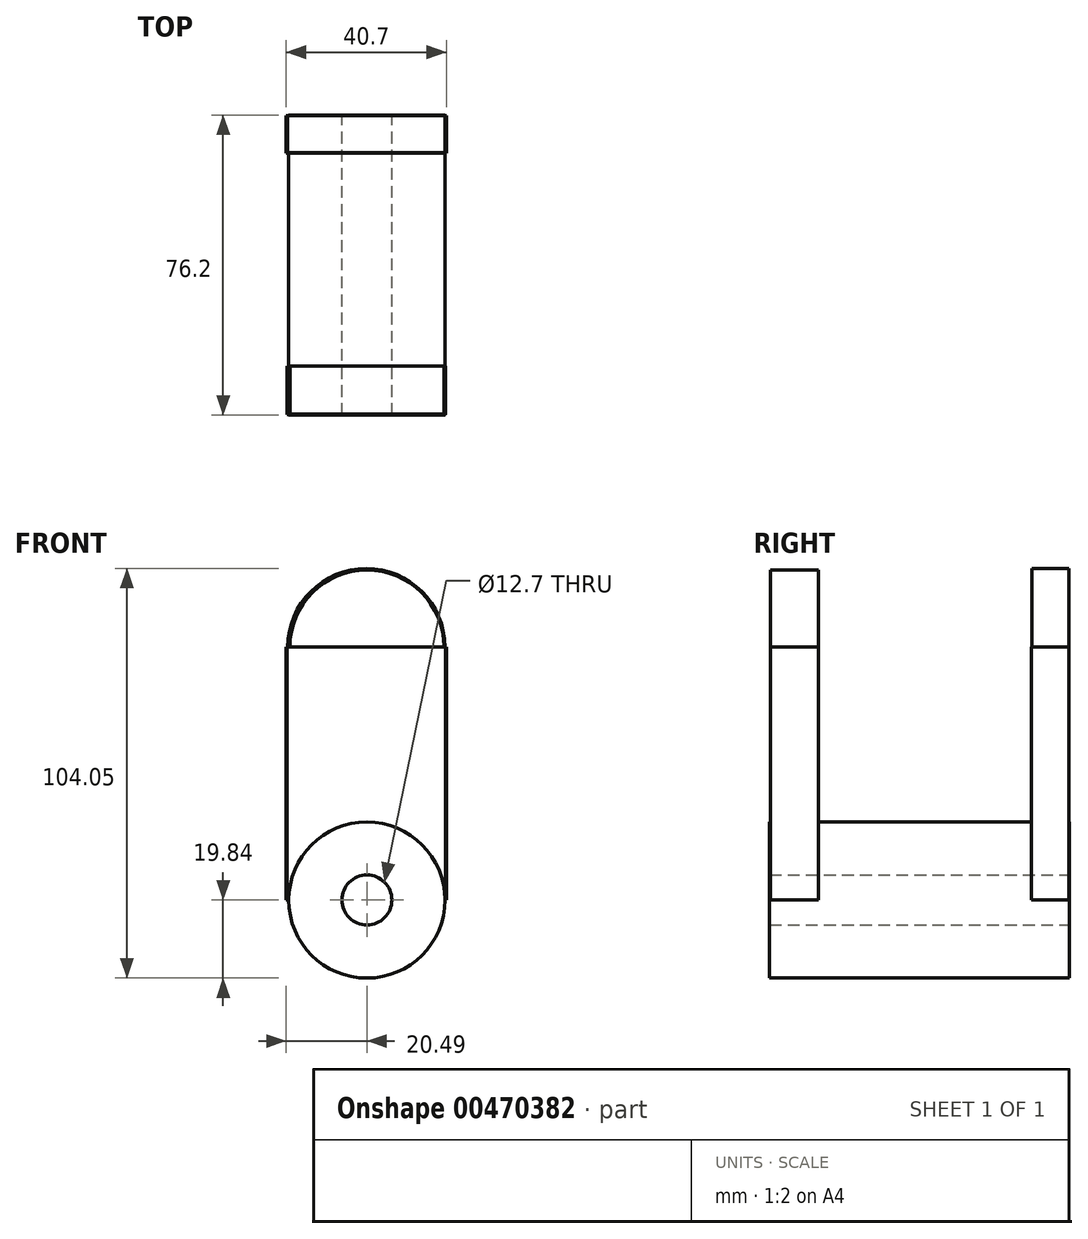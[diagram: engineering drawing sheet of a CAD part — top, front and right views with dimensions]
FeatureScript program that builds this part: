
annotation { "Feature Type Name" : "Feature", "Feature Type Description" : "" }
export const myFeature = defineFeature(function(context is Context, id is Id, definition is map)
    precondition{}
    {
        {
            var Q0;
            Q0=qCreatedBy(makeId("Front.planeOp"),FACE);
            var sketch = newSketch(context, id + "F0", { "sketchPlane" : qUnion([Q0])});
            skCircle(sketch, "E0", {"center": v(0, 0) * mm, "radius": 19.84 * mm});
            skSolve(sketch);
        }
        {
            var Q0;
            Q0 = qSketchRegion(id + "F0", true);
            extrude(context, id + "F1", {"entities" : qUnion([Q0]), "depth" : 76.2 * mm, "symmetric" : true});
        }
        {
            var Q0;
            Q0=makeQuery(id+"F1.opExtrude","CAP_FACE",FACE,{"disambiguationData":[OSD([sQuery(id+"F0.wireOp",EDGE,"E0")])],"isStart":true});
            var sketch = newSketch(context, id + "F2", { "sketchPlane" : qUnion([Q0])});
            skPoint(sketch, "E1", {"position": v(0, 0) * mm});
            skSolve(sketch);
        }
        {
            var Q0;
            Q0=qCreatedBy(makeId("Top.planeOp"),FACE);
            var sketch = newSketch(context, id + "F3", { "sketchPlane" : qUnion([Q0])});
            skLineSegment(sketch, "E2.bottom", {"start": v(-20.21, -37.91) * mm, "end": v(19.93, -37.91) * mm});
            skLineSegment(sketch, "E2.top", {"start": v(-20.21, -25.65) * mm, "end": v(19.93, -25.65) * mm});
            skLineSegment(sketch, "E2.left", {"start": v(-20.21, -37.91) * mm, "end": v(-20.21, -25.65) * mm});
            skLineSegment(sketch, "E2.right", {"start": v(19.93, -37.91) * mm, "end": v(19.93, -25.65) * mm});
            skSolve(sketch);
        }
        {
            var Q0;
            Q0=makeQuery(id+"F3.imprint","IMPRINT",FACE,{"disambiguationData":[TD([[makeQuery(id+"F3.imprint","IMPRINT",EDGE,{"derivedFrom":sQuery(id+"F3.wireOp",EDGE,"E2.bottom")}),1.0]])]});
            extrude(context, id + "F4", {"entities" : qUnion([Q0]), "operationType" : NewBodyOperationType.ADD, "depth" : 64.26 * mm});
        }
        {
            var Q0;
            Q0=qCreatedBy(makeId("Top.planeOp"),FACE);
            var sketch = newSketch(context, id + "F5", { "sketchPlane" : qUnion([Q0])});
            skLineSegment(sketch, "E3.bottom", {"start": v(-20.5, 28.44) * mm, "end": v(20.21, 28.44) * mm});
            skLineSegment(sketch, "E3.top", {"start": v(-20.5, 37.91) * mm, "end": v(20.21, 37.91) * mm});
            skLineSegment(sketch, "E3.left", {"start": v(-20.5, 28.44) * mm, "end": v(-20.5, 37.91) * mm});
            skLineSegment(sketch, "E3.right", {"start": v(20.21, 28.44) * mm, "end": v(20.21, 37.91) * mm});
            skSolve(sketch);
        }
        {
            var Q0;
            Q0 = qSketchRegion(id + "F5", true);
            extrude(context, id + "F6", {"entities" : qUnion([Q0]), "operationType" : NewBodyOperationType.ADD, "depth" : 64.26 * mm});
        }
        {
            var Q0;
            Q0=sQuery(id+"F2.wireOp",VERTEX,"E1");
            var Q1;
            Q1=makeQuery(id+"F1.opExtrude","SWEPT_BODY",BODY,{"disambiguationData":[OSD([sQuery(id+"F0.wireOp",EDGE,"E0")])]});
            hole(context, id + "F7", {"style" : HoleStyle.SIMPLE, "endStyle" : HoleEndStyle.THROUGH, "holeDiameter" : 12.7 * mm, "isTappedThrough" : true, "tappedDepth" : 12.7 * mm, "tapClearance" : 3, "locations" : qUnion([Q0]), "scope" : qUnion([Q1])});
        }
        {
            var Q0;
            Q0=makeQuery(id+"F4.opExtrude","SWEPT_FACE",FACE,{"disambiguationData":[OSD([sQuery(id+"F3.wireOp",EDGE,"E2.top")])]});
            var sketch = newSketch(context, id + "F8", { "sketchPlane" : qUnion([Q0])});
            skCircle(sketch, "E4", {"center": v(0, 64.26) * mm, "radius": 19.57 * mm});
            skLineSegment(sketch, "E5", {"start": v(-19.93, 64.26) * mm, "end": v(20.21, 64.26) * mm});
            skSolve(sketch);
        }
        {
            var Q0;
            {var subQ0=sQuery(id+"F8.wireOp",EDGE,"E5");var subQ1=sQuery(id+"F8.wireOp",EDGE,"E4");var subQ2=makeQuery(id+"F8.imprint","INTERSECT",VERTEX,{"disambiguationData":[OD(0.0)],"derivedFrom":[subQ1,subQ0]});Q0=makeQuery(id+"F8.imprint","IMPRINT",FACE,{"disambiguationData":[TD([[makeQuery(id+"F8.imprint","IMPRINT",EDGE,{"disambiguationData":[TD([[subQ2,-1.0]])],"derivedFrom":subQ1}),1.0]])]});}
            extrude(context, id + "F9", {"entities" : qUnion([Q0]), "operationType" : NewBodyOperationType.ADD, "oppositeDirection" : true, "depth" : 12.2 * mm});
        }
        {
            var Q0;
            Q0=makeQuery(id+"F6.opExtrude","SWEPT_FACE",FACE,{"disambiguationData":[OSD([sQuery(id+"F5.wireOp",EDGE,"E3.top")])]});
            var sketch = newSketch(context, id + "F10", { "sketchPlane" : qUnion([Q0])});
            skArc(sketch, "E6", {"start": v(20.1, 64.26) * mm, "mid": v(0.14, 84.21) * mm, "end": v(-19.81, 64.26) * mm});
            skLineSegment(sketch, "E7", {"start": v(-20.21, 64.26) * mm, "end": v(20.5, 64.26) * mm});
            skSolve(sketch);
        }
        {
            var Q0;
            Q0 = qSketchRegion(id + "F10", true);
            extrude(context, id + "F11", {"entities" : qUnion([Q0]), "operationType" : NewBodyOperationType.ADD, "oppositeDirection" : true, "depth" : 9.4 * mm});
        }
    });
